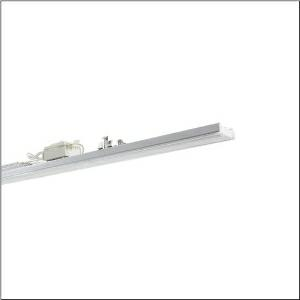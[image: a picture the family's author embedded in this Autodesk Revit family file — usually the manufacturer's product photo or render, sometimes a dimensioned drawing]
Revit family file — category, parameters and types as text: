
# Revit family: licross_21_recessed_mo_52te11dn4axg
name_source: partatom
category: Lighting Fixtures
units: mm (PartAtom-declared; Revit-internal decimal feet)

## family parameters
Cut with Voids When Loaded = No
Host = Face
Light Source = No
Part Type = Normal
Room Calculation Point = No
Round Connector Dimension = Use Diameter
Shared = No

## types (1)
- --- (1 x LED, 10120 lm, 58 W, 4000K)
    Apparent Load = 58 VA
    CIE Flux Codes = 89 96 99 100 100
    Color Rendering = 80
    Color Temperature = 4000K
    Default Elevation = 1800 mm
    Description = Licross 21 Recessed MO, luminaire insert, of sheet steel, galvanised, coil coated, white, length: 1.500mm, width: 66mm, height: 67mm, LED rated luminous flux: 10.120lm, light colour: 840, SDCM (Standard Deviation of Colour Matching)MacAdam ≤ 3 SDCM (initial), control gear: DALI 2, with plug, 5-pole, with phase selection, mains connection: 220..240V, AC, 50/60Hz, rated input power: 58W, internal wiring halogen-free, primary light control with lens, of plastic, primary optical cover: cover, of PMMA, light emission: direct distribution, primary light characteristic: symmetric, protection rating (complete): IP54, insulation class (complete): insulation class I (protective earthing), certification: CE, ENEC, VDE, UKCA, protection symbol: D if used in an environment with non-conductive dust loads with corresponding accessories, impact resistance: IK06, permissible ambient temperature for indoor applications: -25..+35°C, corresponds to IFS (International Featured Standards) requirements for safety and quality in the food industry, reducing of maximum allowable ambient temperature of 5°C with ceiling mounting, LABS conformity tested according to VDMA 24364:2018-05, The light source and the operating device comply with the requirements of the Ecodesign Regulation (EU) 2019/2020 and are replaceable in accordance with this regulation, packaging unit: 1 piece
    Height = 58 mm
    Lamp = 1 x LED
    Lamp Light Flux = 10120 lm
    Lamp Power = 58 W
    Lamp count = 1
    Length = 1500 mm
    Luminous efficacy = 174 lm/W
    Manufacturer = Siteco
    ModVariant = No
    Model = 52TE11DN4AXG
    Mounting Place = Ceiling
    Mounting Type = Pendant
    Number of Poles = 1
    OnlyDefault = Yes
    Power Factor = 1
    Product Name = Licross 21 Recessed MO
    Product group = luminaire insert | ceiling pendant
    ProductGroupID = 901
    Protection Class = Protection class I
    Protection Degree = IP 54
    RLX_Detail_Level = 1
    RLX_Emergency_Light_Flux = 0 lm
    RLX_Emergency_Type = 0
    RLX_Emergency_Type_DB = No
    RlxData = <blob elided: 24769 chars, md5=56250eba>
    Socket = socket
    Standby Power = 0 W
    System Light Flux = 10120 lm
    System Power = 58 W
    Type Comments = factory setting: luminous flux: 100 % | dim-lin: 254 | 390 mA
    Type Image = l_1296930.jpg
    URL = http://relux.com
    VarID = @adj_126973
    Voltage = 0 V
    Weight = 0.00 kg
    Width = 66 mm

## geometry (parser evidence)
native form markers: Blend x4, Sweep x12
no freeform markers — native parametric forms only
